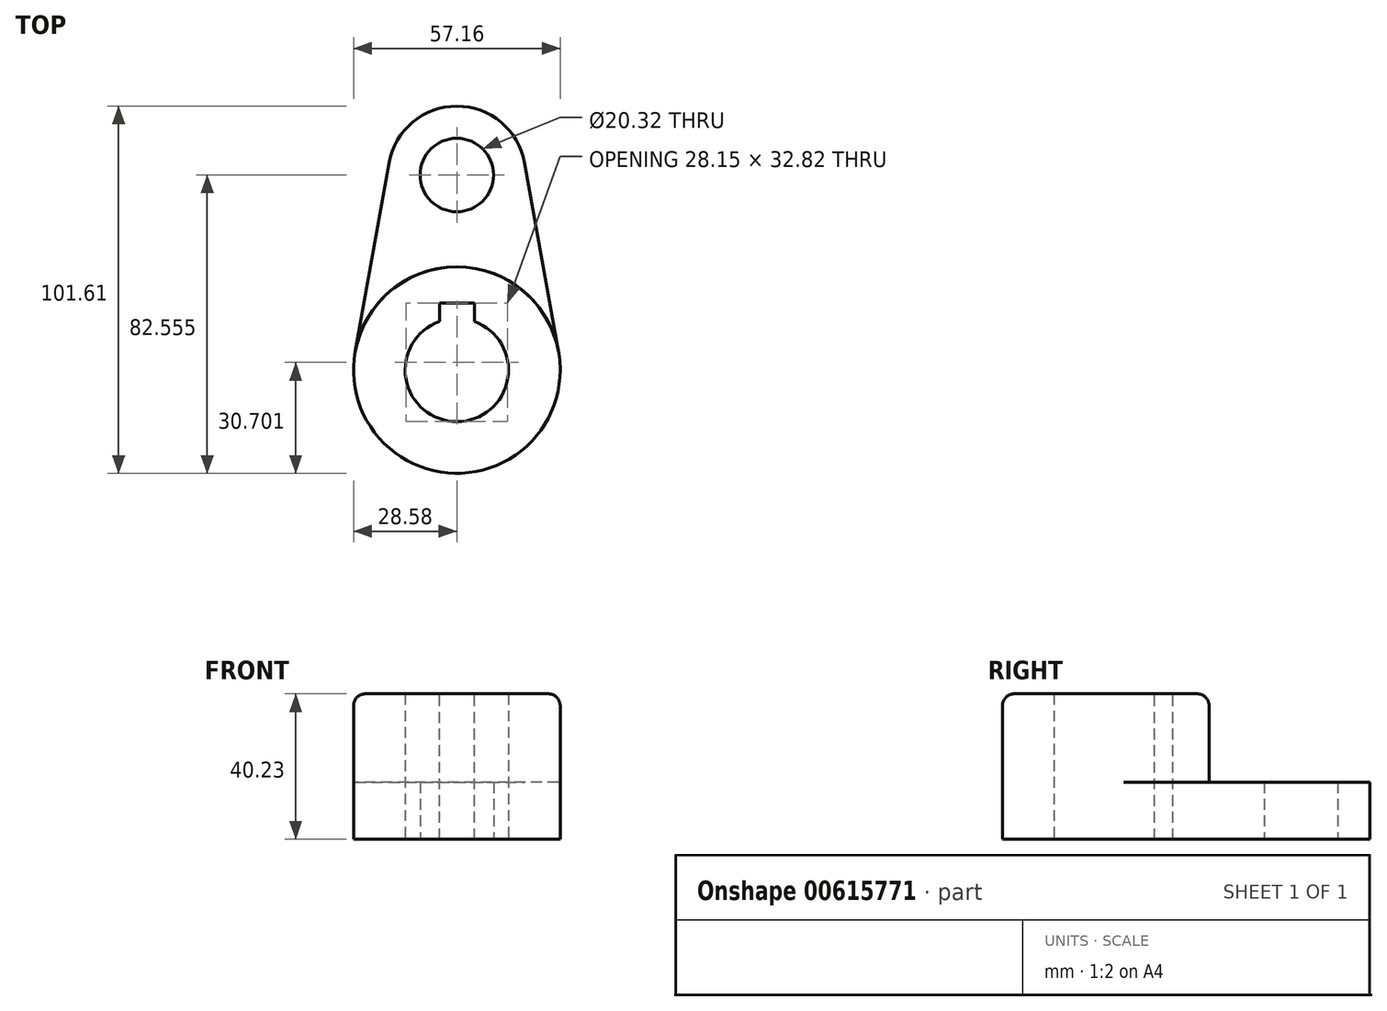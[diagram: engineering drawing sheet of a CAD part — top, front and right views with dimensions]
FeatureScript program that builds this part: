
annotation { "Feature Type Name" : "Feature", "Feature Type Description" : "" }
export const myFeature = defineFeature(function(context is Context, id is Id, definition is map)
    precondition{}
    {
        {
            var Q0;
            Q0=qCreatedBy(makeId("Top.planeOp"),FACE);
            var sketch = newSketch(context, id + "F0", { "sketchPlane" : qUnion([Q0])});
            skCircle(sketch, "E0", {"center": v(0, 0) * mm, "radius": 28.58 * mm});
            skCircle(sketch, "E1", {"center": v(0, 0) * mm, "radius": 14.29 * mm});
            skSolve(sketch);
        }
        {
            var Q0;
            Q0 = qSketchRegion(id + "F0", true);
            extrude(context, id + "F1", {"entities" : qUnion([Q0]), "depth" : 40.23 * mm, "offsetDistance" : 25.4 * mm});
        }
        {
            var Q0;
            Q0=makeQuery(id+"F1.opExtrude","CAP_FACE",FACE,{"disambiguationData":[OSD([sQuery(id+"F0.wireOp",EDGE,"E0"),sQuery(id+"F0.wireOp",EDGE,"E1")])],"isStart":true});
            var sketch = newSketch(context, id + "F2", { "sketchPlane" : qUnion([Q0])});
            skLineSegment(sketch, "E2", {"start": v(0, 0) * mm, "end": v(0, -53.97) * mm, "construction": true});
            skArc(sketch, "E3", {"start": v(-19.05, -53.97) * mm, "mid": v(0, -73.02) * mm, "end": v(19.05, -53.97) * mm});
            skLineSegment(sketch, "E4", {"start": v(-44.75, 0) * mm, "end": v(53.39, 0) * mm, "construction": true});
            skLineSegment(sketch, "E5", {"start": v(0, -53.97) * mm, "end": v(34.97, -53.97) * mm, "construction": true});
            skLineSegment(sketch, "E6", {"start": v(0, -53.98) * mm, "end": v(-35.54, -53.98) * mm, "construction": true});
            skLineSegment(sketch, "E7", {"start": v(-29.03, 0) * mm, "end": v(-18.75, -57.34) * mm});
            skCircle(sketch, "E8", {"center": v(0, -53.97) * mm, "radius": 10.16 * mm});
            skArc(sketch, "E9", {"start": v(-28.58, 0) * mm, "mid": v(0, -28.58) * mm, "end": v(28.58, 0) * mm});
            skArc(sketch, "E10", {"start": v(-18.92, -53.97) * mm, "mid": v(0, -72.9) * mm, "end": v(18.92, -53.97) * mm});
            skLineSegment(sketch, "E11", {"start": v(29.03, 0) * mm, "end": v(18.75, -57.34) * mm});
            skSolve(sketch);
        }
        {
            var Q0;
            Q0 = qSketchRegion(id + "F2", true);
            extrude(context, id + "F3", {"entities" : qUnion([Q0]), "operationType" : NewBodyOperationType.ADD, "oppositeDirection" : true, "depth" : 15.77 * mm, "offsetDistance" : 25.4 * mm});
        }
        {
            var Q0;
            Q0=makeQuery(id+"F1.opExtrude","CAP_FACE",FACE,{"disambiguationData":[OSD([sQuery(id+"F0.wireOp",EDGE,"E0"),sQuery(id+"F0.wireOp",EDGE,"E1")])],"isStart":false});
            var sketch = newSketch(context, id + "F4", { "sketchPlane" : qUnion([Q0])});
            skLineSegment(sketch, "E12", {"start": v(0, 0) * mm, "end": v(0, 31.9) * mm, "construction": true});
            skLineSegment(sketch, "E13.bottom", {"start": v(-4.83, 18.53) * mm, "end": v(4.83, 18.53) * mm});
            skLineSegment(sketch, "E13.top", {"start": v(-4.83, 13.45) * mm, "end": v(4.83, 13.45) * mm});
            skLineSegment(sketch, "E13.left", {"start": v(-4.83, 18.53) * mm, "end": v(-4.83, 13.45) * mm});
            skLineSegment(sketch, "E13.right", {"start": v(4.83, 18.53) * mm, "end": v(4.83, 13.45) * mm});
            skLineSegment(sketch, "E14", {"start": v(0, -14.29) * mm, "end": v(49.12, -14.29) * mm, "construction": true});
            skSolve(sketch);
        }
        {
            var Q0;
            Q0 = qSketchRegion(id + "F4", true);
            extrude(context, id + "F5", {"entities" : qUnion([Q0]), "operationType" : NewBodyOperationType.REMOVE, "endBound" : BoundingType.UP_TO_NEXT, "oppositeDirection" : true, "depth" : 25.4 * mm, "offsetDistance" : 25.4 * mm});
        }
        {
            var Q0;
            Q0=makeQuery(id+"F1.opExtrude","CAP_EDGE",EDGE,{"disambiguationData":[OSD([sQuery(id+"F0.wireOp",EDGE,"E0")])],"isStart":false});
            fillet(context, id + "F6", {"entities" : qUnion([Q0]), "radius" : 3.3 * mm, "tangentPropagation" : true, "allowEdgeOverflow" : false});
        }
    });
